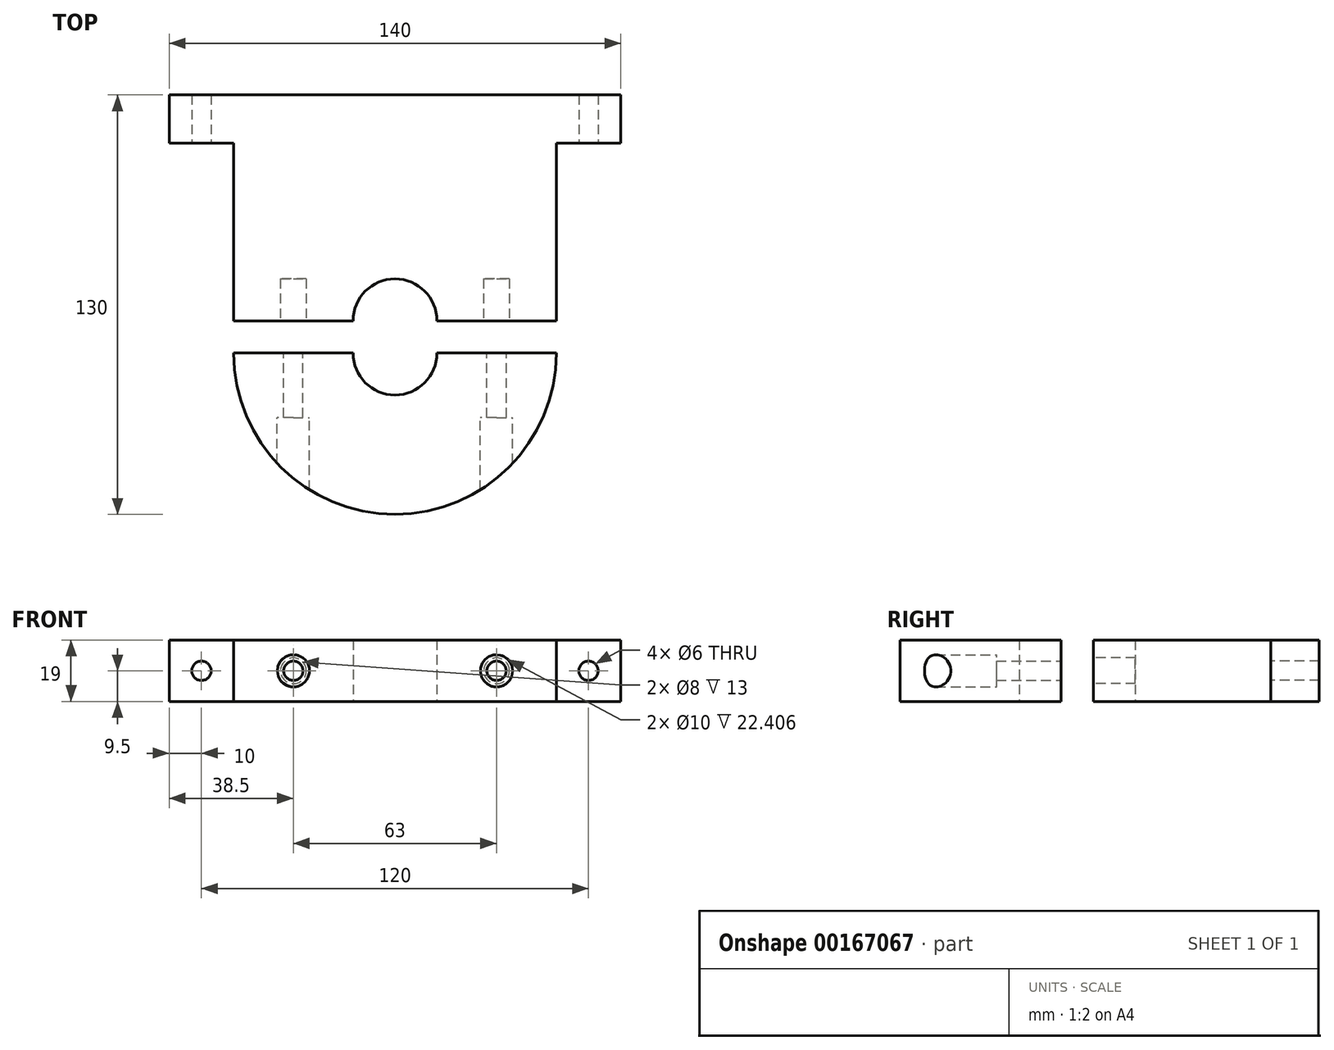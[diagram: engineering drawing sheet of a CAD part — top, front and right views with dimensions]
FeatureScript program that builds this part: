
annotation { "Feature Type Name" : "Feature", "Feature Type Description" : "" }
export const myFeature = defineFeature(function(context is Context, id is Id, definition is map)
    precondition{}
    {
        {
            var Q0;
            Q0=qCreatedBy(makeId("Top.planeOp"),FACE);
            var sketch = newSketch(context, id + "F0", { "sketchPlane" : qUnion([Q0])});
            skArc(sketch, "E0", {"start": v(13, 0) * mm, "mid": v(0, 13) * mm, "end": v(-13, 0) * mm});
            skLineSegment(sketch, "E1", {"start": v(13, 0) * mm, "end": v(50, 0) * mm});
            skLineSegment(sketch, "E2", {"start": v(50, 0) * mm, "end": v(50, 55) * mm});
            skLineSegment(sketch, "E3", {"start": v(-13, 0) * mm, "end": v(-50, 0) * mm});
            skLineSegment(sketch, "E4", {"start": v(-50, 0) * mm, "end": v(-50, 55) * mm});
            skLineSegment(sketch, "E5", {"start": v(-50, 55) * mm, "end": v(-70, 55) * mm});
            skLineSegment(sketch, "E6", {"start": v(-70, 55) * mm, "end": v(-70, 70) * mm});
            skLineSegment(sketch, "E7", {"start": v(-70, 70) * mm, "end": v(70, 70) * mm});
            skLineSegment(sketch, "E8", {"start": v(70, 70) * mm, "end": v(70, 55) * mm});
            skLineSegment(sketch, "E9", {"start": v(70, 55) * mm, "end": v(50, 55) * mm});
            skArc(sketch, "E10", {"start": v(-50, -10) * mm, "mid": v(0, -60) * mm, "end": v(50, -10) * mm});
            skArc(sketch, "E11", {"start": v(-13, -10) * mm, "mid": v(0, -23) * mm, "end": v(13, -10) * mm});
            skLineSegment(sketch, "E12", {"start": v(-50, -10) * mm, "end": v(-13, -10) * mm});
            skLineSegment(sketch, "E13", {"start": v(13, -10) * mm, "end": v(50, -10) * mm});
            skSolve(sketch);
        }
        {
            var Q0;
            Q0=makeQuery(id+"F0.imprint","IMPRINT",FACE,{"disambiguationData":[TD([[makeQuery(id+"F0.imprint","IMPRINT",EDGE,{"derivedFrom":sQuery(id+"F0.wireOp",EDGE,"E0")}),-1.0]])]});
            var Q1;
            Q1=makeQuery(id+"F0.imprint","IMPRINT",FACE,{"disambiguationData":[TD([[makeQuery(id+"F0.imprint","IMPRINT",EDGE,{"derivedFrom":sQuery(id+"F0.wireOp",EDGE,"E10")}),1.0]])]});
            extrude(context, id + "F1", {"entities" : qUnion([Q0, Q1]), "depth" : 19 * mm});
        }
        {
            var Q0;
            Q0=makeQuery(id+"F1.opExtrude","SWEPT_FACE",FACE,{"disambiguationData":[OSD([sQuery(id+"F0.wireOp",EDGE,"E3")])]});
            var sketch = newSketch(context, id + "F2", { "sketchPlane" : qUnion([Q0])});
            skCircle(sketch, "E14", {"center": v(-31.5, 9.5) * mm, "radius": 4 * mm});
            skPoint(sketch, "E14.centerSnap0", {"position": v(-50, 9.5) * mm});
            skCircle(sketch, "E15", {"center": v(31.5, 9.5) * mm, "radius": 4 * mm});
            skSolve(sketch);
        }
        {
            var Q0;
            Q0=makeQuery(id+"F2.imprint","IMPRINT",FACE,{"disambiguationData":[TD([[makeQuery(id+"F2.imprint","IMPRINT",EDGE,{"derivedFrom":sQuery(id+"F2.wireOp",EDGE,"E14")}),1.0]])]});
            var Q1;
            Q1=makeQuery(id+"F2.imprint","IMPRINT",FACE,{"disambiguationData":[TD([[makeQuery(id+"F2.imprint","IMPRINT",EDGE,{"derivedFrom":sQuery(id+"F2.wireOp",EDGE,"E15")}),1.0]])]});
            extrude(context, id + "F3", {"entities" : qUnion([Q0, Q1]), "operationType" : NewBodyOperationType.REMOVE, "oppositeDirection" : true, "depth" : 13 * mm});
        }
        {
            var Q0;
            Q0=makeQuery(id+"F1.opExtrude","SWEPT_FACE",FACE,{"disambiguationData":[OSD([sQuery(id+"F0.wireOp",EDGE,"E5")])]});
            var sketch = newSketch(context, id + "F4", { "sketchPlane" : qUnion([Q0])});
            skCircle(sketch, "E16", {"center": v(-60, 9.5) * mm, "radius": 3 * mm});
            skCircle(sketch, "E17", {"center": v(60, 9.5) * mm, "radius": 3 * mm});
            skSolve(sketch);
        }
        {
            var Q0;
            Q0=makeQuery(id+"F4.imprint","IMPRINT",FACE,{"disambiguationData":[TD([[makeQuery(id+"F4.imprint","IMPRINT",EDGE,{"derivedFrom":sQuery(id+"F4.wireOp",EDGE,"E16")}),1.0]])]});
            var Q1;
            Q1=makeQuery(id+"F4.imprint","IMPRINT",FACE,{"disambiguationData":[TD([[makeQuery(id+"F4.imprint","IMPRINT",EDGE,{"derivedFrom":sQuery(id+"F4.wireOp",EDGE,"E17")}),1.0]])]});
            extrude(context, id + "F5", {"entities" : qUnion([Q0, Q1]), "operationType" : NewBodyOperationType.REMOVE, "oppositeDirection" : true, "depth" : 25 * mm});
        }
        {
            var Q0;
            Q0=makeQuery(id+"F1.opExtrude","SWEPT_FACE",FACE,{"disambiguationData":[OSD([sQuery(id+"F0.wireOp",EDGE,"E13")])]});
            var sketch = newSketch(context, id + "F6", { "sketchPlane" : qUnion([Q0])});
            skCircle(sketch, "E18", {"center": v(-31.5, 9.5) * mm, "radius": 3 * mm});
            skCircle(sketch, "E19", {"center": v(31.5, 9.5) * mm, "radius": 3 * mm});
            skSolve(sketch);
        }
        {
            var Q0;
            Q0=makeQuery(id+"F6.imprint","IMPRINT",FACE,{"disambiguationData":[TD([[makeQuery(id+"F6.imprint","IMPRINT",EDGE,{"derivedFrom":sQuery(id+"F6.wireOp",EDGE,"E18")}),1.0]])]});
            var Q1;
            Q1=makeQuery(id+"F6.imprint","IMPRINT",FACE,{"disambiguationData":[TD([[makeQuery(id+"F6.imprint","IMPRINT",EDGE,{"derivedFrom":sQuery(id+"F6.wireOp",EDGE,"E19")}),1.0]])]});
            extrude(context, id + "F7", {"entities" : qUnion([Q0, Q1]), "operationType" : NewBodyOperationType.REMOVE, "oppositeDirection" : true, "depth" : 42 * mm});
        }
        {
            var Q0;
            Q0=qCreatedBy(makeId("Front.planeOp"),FACE);
            cPlane(context, id + "F8", {"entities" : qUnion([Q0]), "cplaneType" : CPlaneType.OFFSET, "offset" : 30 * mm, "width" : 150 * mm, "height" : 150 * mm});
        }
        {
            var Q0;
            Q0=qCreatedBy(id+"F8.planeOp",FACE);
            var sketch = newSketch(context, id + "F9", { "sketchPlane" : qUnion([Q0])});
            skCircle(sketch, "E20", {"center": v(-31.5, 9.5) * mm, "radius": 5 * mm});
            skCircle(sketch, "E21", {"center": v(31.5, 9.5) * mm, "radius": 5 * mm});
            skSolve(sketch);
        }
        {
            var Q0;
            Q0=makeQuery(id+"F9.imprint","IMPRINT",FACE,{"disambiguationData":[TD([[makeQuery(id+"F9.imprint","IMPRINT",EDGE,{"derivedFrom":sQuery(id+"F9.wireOp",EDGE,"E20")}),1.0]])]});
            var Q1;
            Q1=makeQuery(id+"F9.imprint","IMPRINT",FACE,{"disambiguationData":[TD([[makeQuery(id+"F9.imprint","IMPRINT",EDGE,{"derivedFrom":sQuery(id+"F9.wireOp",EDGE,"E21")}),1.0]])]});
            extrude(context, id + "F10", {"entities" : qUnion([Q0, Q1]), "operationType" : NewBodyOperationType.REMOVE, "depth" : 25 * mm});
        }
    });
